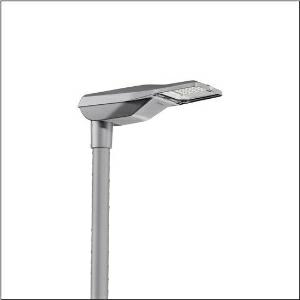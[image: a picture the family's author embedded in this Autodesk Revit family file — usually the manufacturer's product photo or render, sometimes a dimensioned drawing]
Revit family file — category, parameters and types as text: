
# Revit family: streetlight_sl_21_iq_micro___st1_0a_5xe1d41d08cb_ed56
name_source: partatom
category: Lighting Fixtures
units: mm (PartAtom-declared; Revit-internal decimal feet)

## family parameters
Cut with Voids When Loaded = No
Host = Face
Light Source = No
Part Type = Normal
Room Calculation Point = No
Round Connector Dimension = Use Diameter
Shared = No

## types (1)
- --- (1 x LED, 2980 lm, 19.4 W, 4000K)
    Apparent Load = 19 VA
    CIE Flux Codes = 37 72 97 100 100
    Color Rendering = 70
    Color Temperature = 4000K
    Default Elevation = 1800 mm
    Description = Streetlight SL 21 iQ micro, mast luminaire, primary light control with lens, of PMMA, primary optical cover: cover, of toughened safety glass, transparent, light distribution: ST1.0a, light emission: direct distribution, primary light characteristic: asymmetric, installation type: post-top, side-entry, LED, High Power LED, rated luminous flux: 2.980lm, luminous efficacy: 154lm/W, light colour: 740, colour temperature: 4000K, control gear: iQ-Comfort, control: Auto-Match, Temp-Guard, Lumen-Switch, Night-Set, Smart-Wire, Light-Fading, Desk-Remote (wireless, voltage-free reading and setting of iQ features in the workshop via application-optimized NFC function/RFID function), optimised constant luminous flux control (CLO 2.0), pre-setting: linear dimming characteristic, mains connection: 220..240V, AC, 50/60Hz, start of lifetime: 19W, end of service life: 20W, reduction: 10W, luminaire housing, of diecast aluminium, powder-coated, Siteco® metallic grey (DB 702S), corrosivity category C5 mid according to DIN EN ISO 12944, please order mast flange separately, inclination adjustable: 0°, 5°, 10°, 15°, sealing non-destructively replaceable, multi-level sealing system, length: 528mm, width: 235mm, height: 110mm, mast flange for spigot size: 42mm (side-entry): 5XC10008XM4, 60/48mm (side-entry/post-top): 5XC10108XM2, 76/60mm (side-entry/post-top): 5XC10108XM1, protection rating (complete): IP66, insulation class (complete): insulation class II (safety insulation), certification: CE, ENEC, ENEC+, VDE, impact resistance: IK10, permissible operating ambient temperature for outdoor applications: -40..+50°C, standard-compliant lighting for roads and squares, packaging unit: 1 piece

Light Distribution: ST1.0a
    Height = 110 mm
    Lamp = 1 x LED
    Lamp Light Flux = 2980 lm
    Lamp Power = 19.4 W
    Lamp count = 1
    Length = 528 mm
    Luminous efficacy = 154 lm/W
    Manufacturer = Siteco
    ModVariant = No
    Model = 5XE1D41D08CB
    Number of Poles = 1
    OnlyDefault = Yes
    Power Factor = 1
    Product Name = Streetlight SL 21 iQ micro | ST1.0a
    Product group = mast luminaire | pylon top
    ProductGroupID = 6100
    Protection Class = Protection class II
    Protection Degree = IP 66
    RLX_Detail_Level = 1
    RLX_Emergency_Light_Flux = 0 lm
    RLX_Emergency_Type = 0
    RLX_Emergency_Type_DB = No
    RlxData = <blob elided: 98389 chars, md5=9bc4db3d>
    Socket = socket
    Standby Power = 0 W
    System Light Flux = 2980 lm
    System Power = 19 W
    Type Comments = factory setting: luminous flux: 100 % | dim-lin: 254 | 387 mA
    Type Image = l_1006881.jpg
    URL = http://relux.com
    VarID = @adj_160695
    Voltage = 0 V
    Weight = 0.00 kg
    Width = 235 mm

## geometry (parser evidence)
native form markers: Blend x4, Sweep x11
no freeform markers — native parametric forms only
